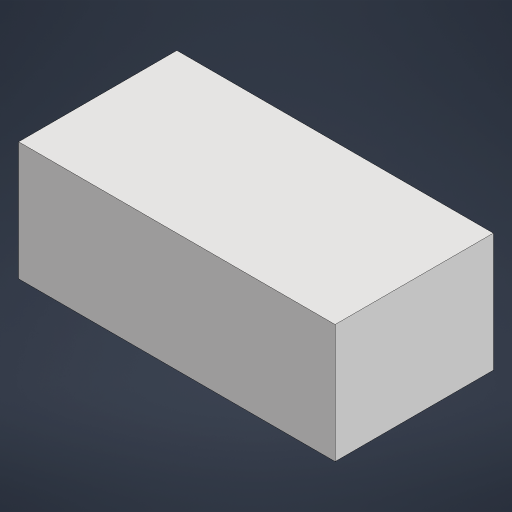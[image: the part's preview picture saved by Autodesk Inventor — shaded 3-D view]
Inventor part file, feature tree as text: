
AUTODESK INVENTOR PART (.ipt)
format: ipt  version: 2023.1 (Build 271208000, 208)  size: 137,216 bytes
history: native  units: in
note: dims shown in document units (in); Inventor stores cm internally (conversion verified against a paired STEP export)
features: extrude x1, sketch x1
ambient origin geometry x8: Origin, YZ Plane, XZ Plane, XY Plane, X Axis, Y Axis, Z Axis, Center Point
bodies: Solid1 (feature_tree)
feature tree (2):
  extrude  "Extrusion1"  Depth=4.0in
  sketch  "Sketch2"  dims[d3=8.0in d4=4.0in d5=3.0in d6=0.0in]
